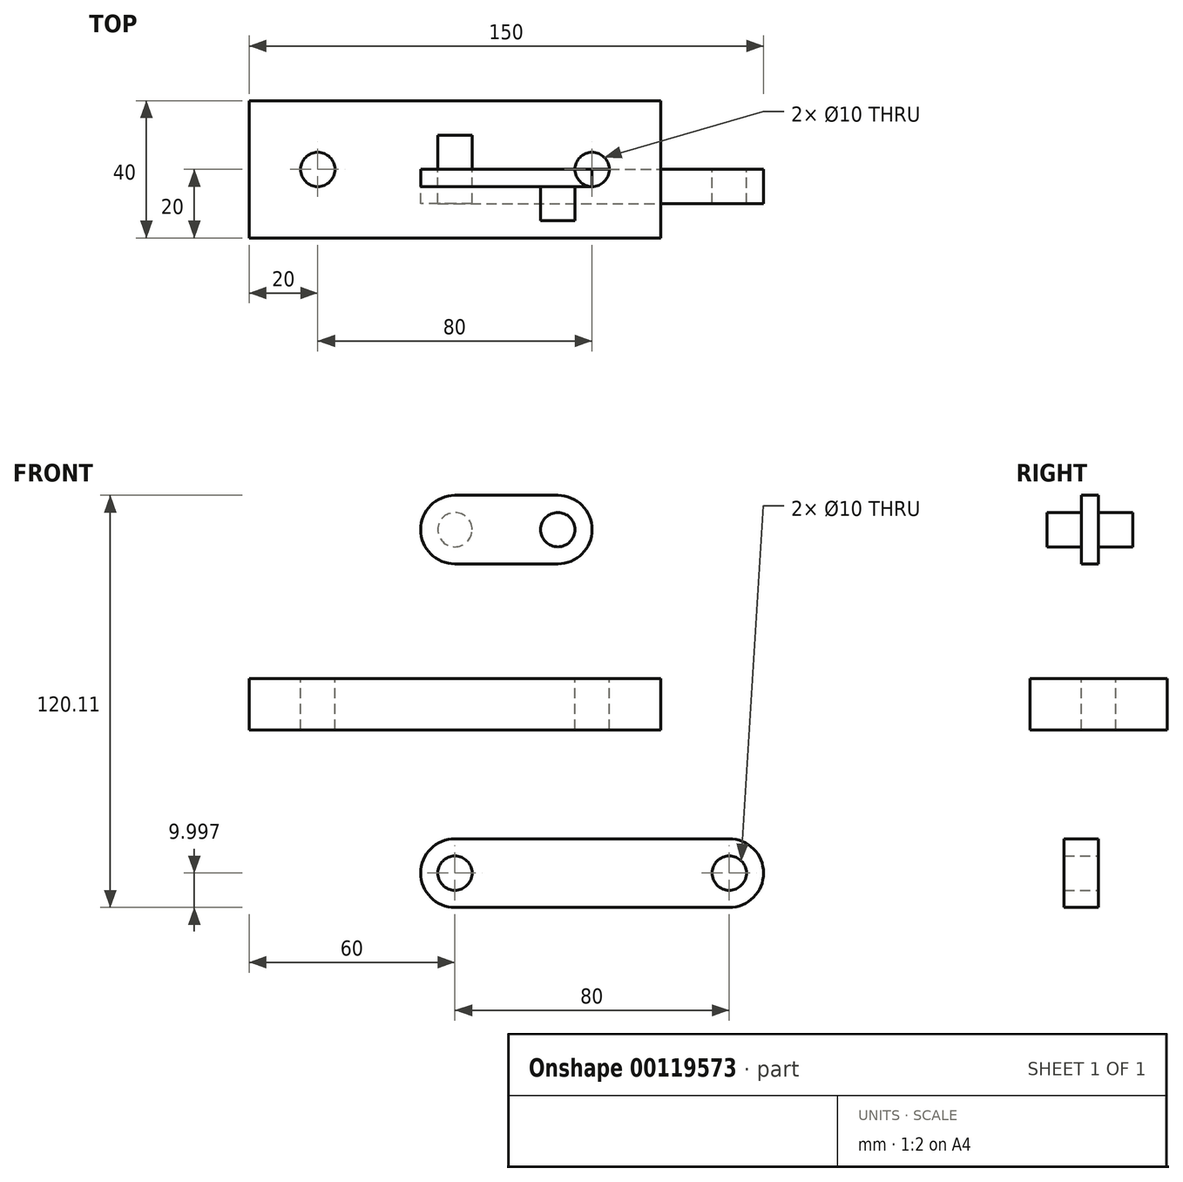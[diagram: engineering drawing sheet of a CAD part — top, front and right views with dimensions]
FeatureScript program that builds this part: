
annotation { "Feature Type Name" : "Feature", "Feature Type Description" : "" }
export const myFeature = defineFeature(function(context is Context, id is Id, definition is map)
    precondition{}
    {
        {
            var Q0;
            Q0=qCreatedBy(makeId("Top.planeOp"),FACE);
            var sketch = newSketch(context, id + "F0", { "sketchPlane" : qUnion([Q0])});
            skLineSegment(sketch, "E0.bottom", {"start": v(60, -20) * mm, "end": v(-60, -20) * mm});
            skLineSegment(sketch, "E0.top", {"start": v(60, 20) * mm, "end": v(-60, 20) * mm});
            skLineSegment(sketch, "E0.left", {"start": v(60, -20) * mm, "end": v(60, 20) * mm});
            skLineSegment(sketch, "E0.right", {"start": v(-60, -20) * mm, "end": v(-60, 20) * mm});
            skPoint(sketch, "E0.middle", {"position": v(0, 0) * mm});
            skCircle(sketch, "E1", {"center": v(-40, 0) * mm, "radius": 5 * mm});
            skCircle(sketch, "E2", {"center": v(40, 0) * mm, "radius": 5 * mm});
            skSolve(sketch);
        }
        {
            var Q0;
            Q0 = qSketchRegion(id + "F0", true);
            extrude(context, id + "F1", {"entities" : qUnion([Q0]), "oppositeDirection" : true, "depth" : 15 * mm});
        }
        {
            var Q0;
            Q0=qCreatedBy(makeId("Front.planeOp"),FACE);
            var sketch = newSketch(context, id + "F2", { "sketchPlane" : qUnion([Q0])});
            skLineSegment(sketch, "E3", {"start": v(0, 53.36) * mm, "end": v(30, 53.36) * mm});
            skLineSegment(sketch, "E4", {"start": v(0, 33.36) * mm, "end": v(30, 33.36) * mm});
            skArc(sketch, "E5", {"start": v(0, 53.36) * mm, "mid": v(-10, 43.36) * mm, "end": v(0, 33.36) * mm});
            skArc(sketch, "E6", {"start": v(30, 53.36) * mm, "mid": v(40, 43.36) * mm, "end": v(30, 33.36) * mm});
            skCircle(sketch, "E7", {"center": v(30, 43.36) * mm, "radius": 5 * mm});
            skCircle(sketch, "E8", {"center": v(0, 43.36) * mm, "radius": 5 * mm});
            skSolve(sketch);
        }
        {
            var Q0;
            Q0=makeQuery(id+"F2.imprint","IMPRINT",FACE,{"disambiguationData":[TD([[makeQuery(id+"F2.imprint","IMPRINT",EDGE,{"derivedFrom":sQuery(id+"F2.wireOp",EDGE,"E3")}),-1.0]])]});
            var Q1;
            Q1=makeQuery(id+"F2.imprint","IMPRINT",FACE,{"disambiguationData":[TD([[makeQuery(id+"F2.imprint","IMPRINT",EDGE,{"derivedFrom":sQuery(id+"F2.wireOp",EDGE,"E7")}),1.0]])]});
            var Q2;
            Q2=makeQuery(id+"F2.imprint","IMPRINT",FACE,{"disambiguationData":[TD([[makeQuery(id+"F2.imprint","IMPRINT",EDGE,{"derivedFrom":sQuery(id+"F2.wireOp",EDGE,"E8")}),1.0]])]});
            extrude(context, id + "F3", {"entities" : qUnion([Q0, Q1, Q2]), "depth" : 5 * mm});
        }
        {
            var Q0;
            Q0=makeQuery(id+"F2.imprint","IMPRINT",FACE,{"disambiguationData":[TD([[makeQuery(id+"F2.imprint","IMPRINT",EDGE,{"derivedFrom":sQuery(id+"F2.wireOp",EDGE,"E7")}),1.0]])]});
            extrude(context, id + "F4", {"entities" : qUnion([Q0]), "operationType" : NewBodyOperationType.ADD, "depth" : 15 * mm});
        }
        {
            var Q0;
            Q0=makeQuery(id+"F2.imprint","IMPRINT",FACE,{"disambiguationData":[TD([[makeQuery(id+"F2.imprint","IMPRINT",EDGE,{"derivedFrom":sQuery(id+"F2.wireOp",EDGE,"E8")}),1.0]])]});
            extrude(context, id + "F5", {"entities" : qUnion([Q0]), "operationType" : NewBodyOperationType.ADD, "oppositeDirection" : true, "depth" : 10 * mm});
        }
        {
            var Q0;
            Q0=qCreatedBy(makeId("Front.planeOp"),FACE);
            var sketch = newSketch(context, id + "F6", { "sketchPlane" : qUnion([Q0])});
            skLineSegment(sketch, "E9", {"start": v(0, -46.75) * mm, "end": v(80, -46.75) * mm});
            skLineSegment(sketch, "E10", {"start": v(0, -66.75) * mm, "end": v(80, -66.75) * mm});
            skArc(sketch, "E11", {"start": v(0, -46.75) * mm, "mid": v(-10, -56.75) * mm, "end": v(0, -66.75) * mm});
            skArc(sketch, "E12", {"start": v(80, -46.75) * mm, "mid": v(90, -56.75) * mm, "end": v(80, -66.75) * mm});
            skCircle(sketch, "E13", {"center": v(80, -56.75) * mm, "radius": 5 * mm});
            skCircle(sketch, "E14", {"center": v(0, -56.75) * mm, "radius": 5 * mm});
            skSolve(sketch);
        }
        {
            var Q0;
            Q0=makeQuery(id+"F6.imprint","IMPRINT",FACE,{"disambiguationData":[TD([[makeQuery(id+"F6.imprint","IMPRINT",EDGE,{"derivedFrom":sQuery(id+"F6.wireOp",EDGE,"E9")}),-1.0]])]});
            extrude(context, id + "F7", {"entities" : qUnion([Q0]), "depth" : 10 * mm});
        }
    });
